# Revit family: Showerhead-Waterworks-Universal-2_75in
name_source: partatom
category: Plumbing Fixtures
revit_build: Autodesk Revit MEP 2014 (Build: 20140709_2115(x64)
units: mm (PartAtom-declared; Revit-internal decimal feet)

## types (17) — shared parameters
ADA Compliant = No
Assembly Code = D2010710
CW Connection = Yes
Certification IAPMO = Yes
Certification State of MA = Yes
Certification cUPC = Yes
Code Compliance = Code # WWSH38: Certified with CEC
Default Elevation = 6' - 6"
Depth = 0' - 2 13/16"
Diameter of Head = 0' - 2 3/4"
Domestic Water Flow Rate = 2 GPM
HW Connection = Yes
Height = 0' - 3 15/16"
Inlet Connection Diameter = 0' - 0 1/2"
Keynote = 22 40 00
Length = 0' - 3 3/4"
Manufacturer = Waterworks
Model = UNSH38
Pressure = 45.00 psi
Product Documentation Link = http://assets.waterworks.com
Product Page URL = http://www.waterworks.com
URL = http://www.waterworks.com
Vent Connection = No
Version = 2014 - v1.0a
Warranty = http://www.waterworks.com
Waste Connection = No
Water Connector = Inlet - Female NPT
Water Pressure = Max: 85psi / Min: 20psi / Recommended: 45psi
‌Installation Requirements or Notes = Shower Arm Sold Separately
zero-valued in all types: CWFU, HWFU, WFU

## per-type parameters (varying)
| type | Constraint | Description | Finish | Model SKU | Product Name |
| Antique Brass | 1 | Universal 2 3/4” Shower Head with Adjustable Spray in Antique Brass | Metal - Waterworks - Antique Brass | 05-18548-02923 | Universal 2 3/4” Shower Head with Adjustable Spray in Antique Brass |
| Antique Copper | 2 | Universal 2 3/4” Shower Head with Adjustable Spray in Antique Copper | Metal - Waterworks - Antique Copper | 05-53358-11855 | Universal 2 3/4” Shower Head with Adjustable Spray in Antique Copper |
| Architectural Bronze | 3 | Universal 2 3/4” Shower Head with Adjustable Spray in Architectural Bronze | Metal - Waterworks - Architectural Bronze | 05-75225-63026 | Universal 2 3/4” Shower Head with Adjustable Spray in Architectural Bronze |
| Burnished Brass | 4 | Universal 2 3/4” Shower Head with Adjustable Spray in Burnished Brass | Metal - Waterworks - Burnished Brass | 05-77155-60594 | Universal 2 3/4” Shower Head with Adjustable Spray in Burnished Brass |
| Burnished Nickel | 5 | Universal 2 3/4” Shower Head with Adjustable Spray in Burnished Nickel | Metal - Waterworks - Burnished Nickel | 05-76930-17424 | Universal 2 3/4” Shower Head with Adjustable Spray in Burnished Nickel |
| Carbon | 6 | Universal 2 3/4” Shower Head with Adjustable Spray in Carbon | Metal - Waterworks - Carbon | 05-34647-92214 | Universal 2 3/4” Shower Head with Adjustable Spray in Carbon |
| Chrome | 7 | Universal 2 3/4” Shower Head with Adjustable Spray in Chrome | Metal - Waterworks - Chrome | 05-43500-65118 | Universal 2 3/4” Shower Head with Adjustable Spray in Chrome |
| Gold | 8 | Universal 2 3/4” Shower Head with Adjustable Spray in Gold | Metal - Waterworks - Gold | 05-12780-88950 | Universal 2 3/4” Shower Head with Adjustable Spray in Gold |
| Graphite | 9 | Universal 2 3/4” Shower Head with Adjustable Spray in Graphite | Metal - Waterworks - Graphite | 05-75586-63935 | Universal 2 3/4” Shower Head with Adjustable Spray in Graphite |
| Matte Gold | 10 | Universal 2 3/4” Shower Head with Adjustable Spray in Matte Gold | Metal - Waterworks - Matte Gold | 05-52928-13061 | Universal 2 3/4” Shower Head with Adjustable Spray in Matte Gold |
| Matte Nickel | 11 | Universal 2 3/4” Shower Head with Adjustable Spray in Matte Nickel | Metal - Waterworks - Matte Nickel | 05-42239-67035 | Universal 2 3/4” Shower Head with Adjustable Spray in Matte Nickel |
| Nickel | 12 | Universal 2 3/4” Shower Head with Adjustable Spray in Nickel | Metal - Waterworks - Nickel | 05-89809-47102 | Universal 2 3/4” Shower Head with Adjustable Spray in Nickel |
| Pewter | 13 | Universal 2 3/4” Shower Head with Adjustable Spray in Pewter | Metal - Waterworks - Pewter | 05-59711-56698 | Universal 2 3/4” Shower Head with Adjustable Spray in Pewter |
| Shiny Copper | 14 | Universal 2 3/4” Shower Head with Adjustable Spray in Shiny Copper | Metal - Waterworks - Shiny Copper | 05-91574-31111 | Universal 2 3/4” Shower Head with Adjustable Spray in Shiny Copper |
| Sovereign | 15 | Universal 2 3/4” Shower Head with Adjustable Spray in Sovereign | Metal - Waterworks - Sovereign | 05-82963-54257 | Universal 2 3/4” Shower Head with Adjustable Spray in Sovereign |
| Unlacquered Brass | 16 | Universal 2 3/4” Shower Head with Adjustable Spray in Unlacquered Brass | Metal - Waterworks - Unlacquered Brass | 05-46723-71070 | Universal 2 3/4” Shower Head with Adjustable Spray in Unlacquered Brass |
| Vintage Brass | 17 | Universal 2 3/4” Shower Head with Adjustable Spray in Vintage Brass | Metal - Waterworks - Vintage Brass | 05-28501-65856 | Universal 2 3/4” Shower Head with Adjustable Spray in Vintage Brass |

## geometry (parser evidence)
native form markers: Sweep x1
no freeform markers — native parametric forms only
